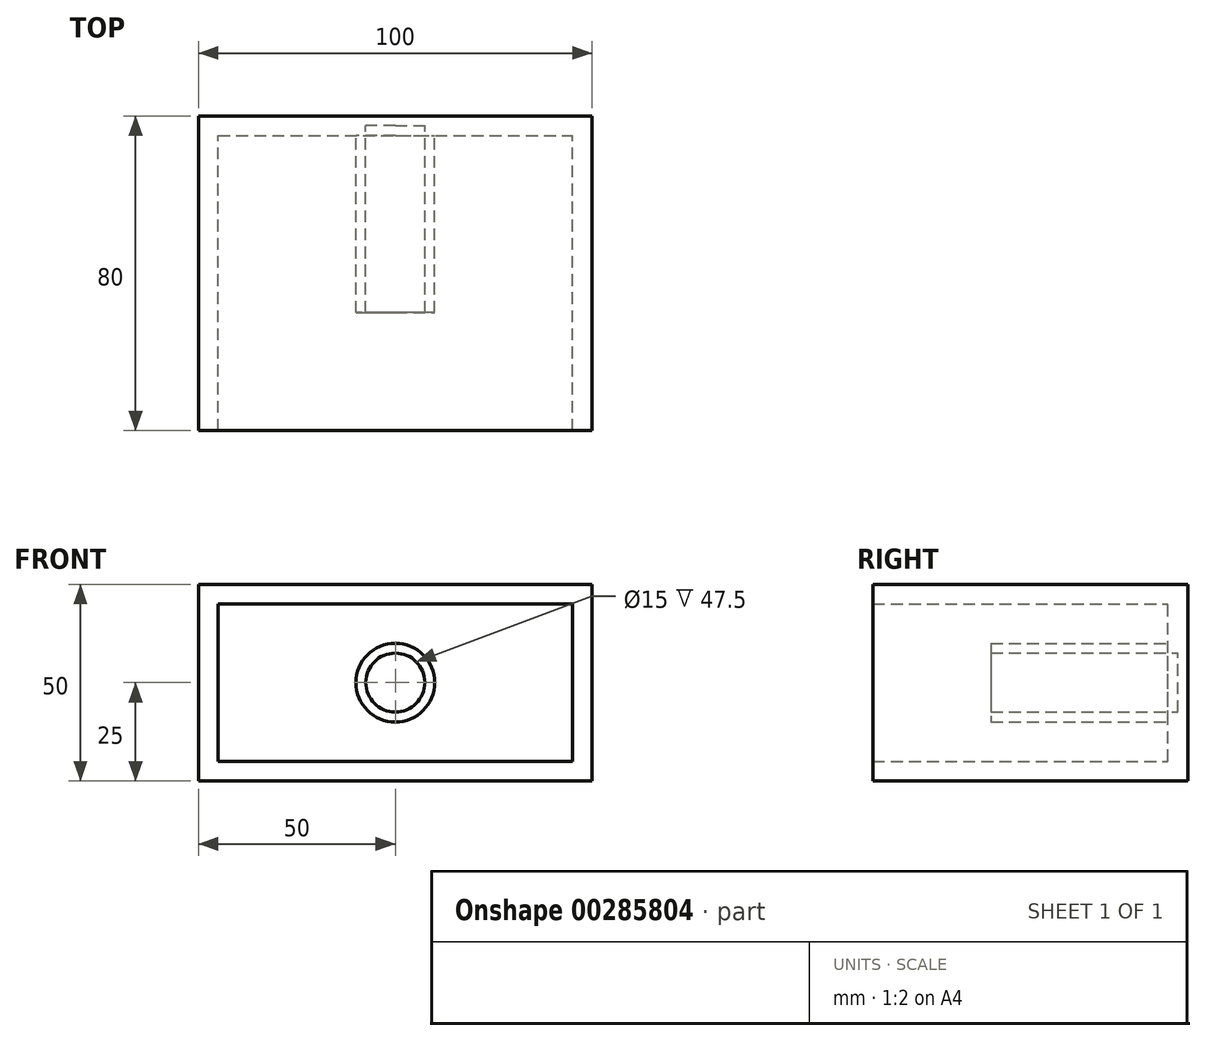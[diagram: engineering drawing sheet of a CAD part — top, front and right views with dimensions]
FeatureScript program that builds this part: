
annotation { "Feature Type Name" : "Feature", "Feature Type Description" : "" }
export const myFeature = defineFeature(function(context is Context, id is Id, definition is map)
    precondition{}
    {
        {
            var Q0;
            Q0=qCreatedBy(makeId("Front.planeOp"),FACE);
            var sketch = newSketch(context, id + "F0", { "sketchPlane" : qUnion([Q0])});
            skLineSegment(sketch, "E0.bottom", {"start": v(-50, -25) * mm, "end": v(50, -25) * mm});
            skLineSegment(sketch, "E0.top", {"start": v(-50, 25) * mm, "end": v(50, 25) * mm});
            skLineSegment(sketch, "E0.left", {"start": v(-50, -25) * mm, "end": v(-50, 25) * mm});
            skLineSegment(sketch, "E0.right", {"start": v(50, -25) * mm, "end": v(50, 25) * mm});
            skPoint(sketch, "E0.middle", {"position": v(0, 0) * mm});
            skSolve(sketch);
        }
        {
            var Q0;
            Q0 = qSketchRegion(id + "F0", true);
            extrude(context, id + "F1", {"entities" : qUnion([Q0]), "depth" : 80 * mm});
        }
        {
            var Q0;
            Q0=makeQuery(id+"F1.opExtrude","CAP_FACE",FACE,{"disambiguationData":[OSD([sQuery(id+"F0.wireOp",EDGE,"E0.bottom"),sQuery(id+"F0.wireOp",EDGE,"E0.top"),sQuery(id+"F0.wireOp",EDGE,"E0.left"),sQuery(id+"F0.wireOp",EDGE,"E0.right")])],"isStart":false});
            shell(context, id + "F2", {"entities" : qUnion([Q0]), "thickness" : 5 * mm});
        }
        {
            var Q0;
            Q0=makeQuery(id+"F1.opExtrude","CAP_FACE",FACE,{"disambiguationData":[OSD([sQuery(id+"F0.wireOp",EDGE,"E0.bottom"),sQuery(id+"F0.wireOp",EDGE,"E0.top"),sQuery(id+"F0.wireOp",EDGE,"E0.left"),sQuery(id+"F0.wireOp",EDGE,"E0.right")])],"isStart":true});
            var sketch = newSketch(context, id + "F3", { "sketchPlane" : qUnion([Q0])});
            skCircle(sketch, "E1", {"center": v(0, 0) * mm, "radius": 10 * mm});
            skSolve(sketch);
        }
        {
            var Q0;
            Q0 = qSketchRegion(id + "F3", true);
            extrude(context, id + "F4", {"entities" : qUnion([Q0]), "operationType" : NewBodyOperationType.ADD, "oppositeDirection" : true, "depth" : 50 * mm});
        }
        {
            var Q0;
            Q0=makeQuery(id+"F4.opExtrude","CAP_FACE",FACE,{"disambiguationData":[OSD([sQuery(id+"F3.wireOp",EDGE,"E1")])],"isStart":false});
            shell(context, id + "F5", {"entities" : qUnion([Q0]), "thickness" : 2.5 * mm});
        }
    });
